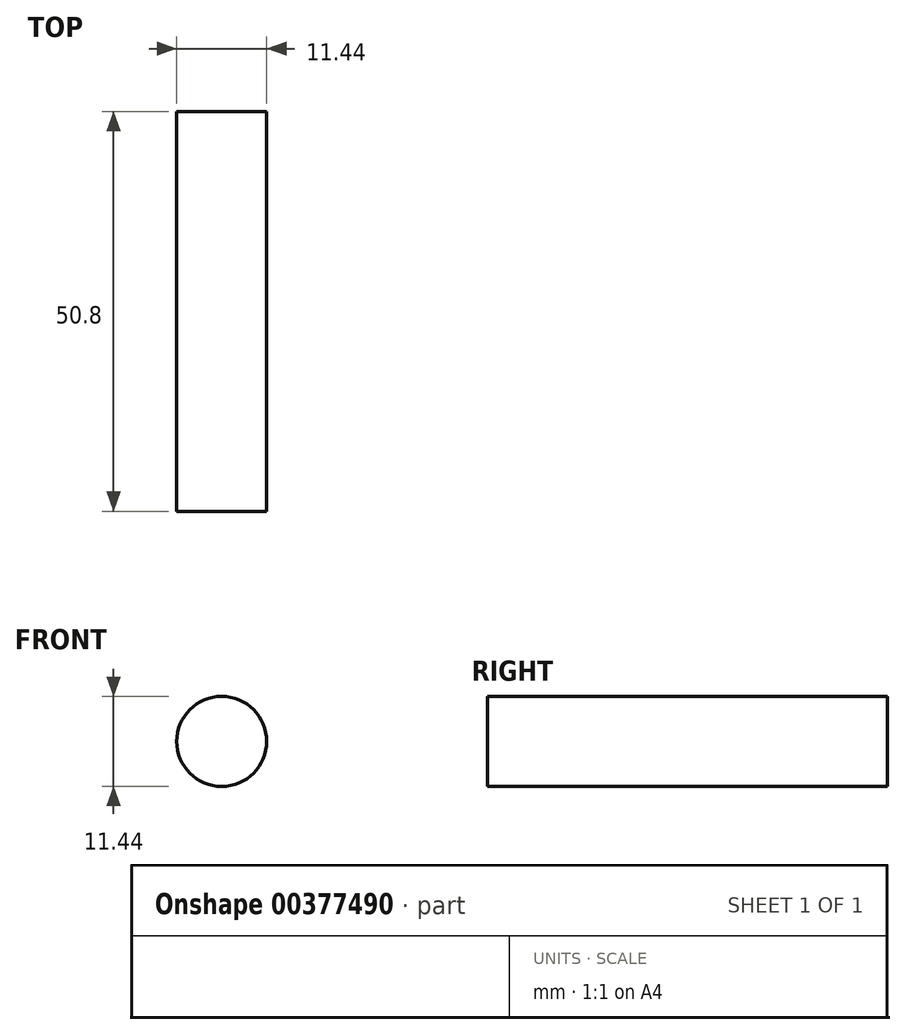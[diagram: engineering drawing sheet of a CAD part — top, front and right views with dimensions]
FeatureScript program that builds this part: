
annotation { "Feature Type Name" : "Feature", "Feature Type Description" : "" }
export const myFeature = defineFeature(function(context is Context, id is Id, definition is map)
    precondition{}
    {
        {
            var Q0;
            Q0=qCreatedBy(makeId("Front.planeOp"),FACE);
            var sketch = newSketch(context, id + "F0", { "sketchPlane" : qUnion([Q0])});
            skCircle(sketch, "E0", {"center": v(0, 0) * mm, "radius": 5.71 * mm});
            skSolve(sketch);
        }
        {
            var Q0;
            Q0 = qSketchRegion(id + "F0", true);
            extrude(context, id + "F1", {"entities" : qUnion([Q0]), "depth" : 50.8 * mm});
        }
    });
